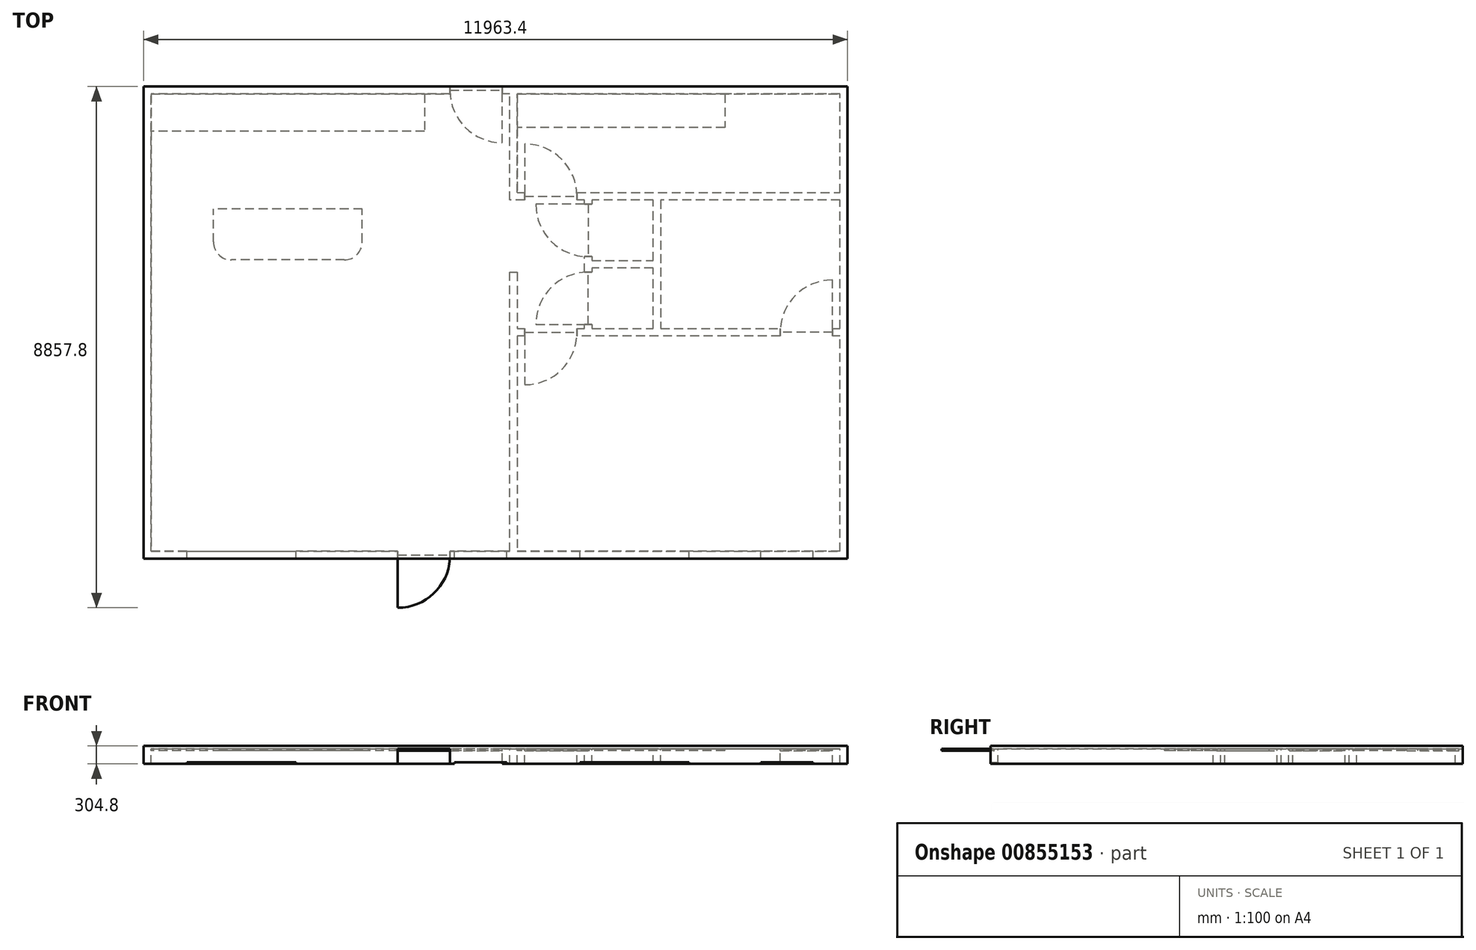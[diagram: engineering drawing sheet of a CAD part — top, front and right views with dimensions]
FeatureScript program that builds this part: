
annotation { "Feature Type Name" : "Feature", "Feature Type Description" : "" }
export const myFeature = defineFeature(function(context is Context, id is Id, definition is map)
    precondition{}
    {
        {
            var Q0;
            Q0=qCreatedBy(makeId("Top.planeOp"),FACE);
            var sketch = newSketch(context, id + "F0", { "sketchPlane" : qUnion([Q0])});
            skLineSegment(sketch, "E0", {"start": v(127, 127) * mm, "end": v(127, 7899.4) * mm});
            skLineSegment(sketch, "E1", {"start": v(127, 7899.4) * mm, "end": v(5207, 7899.4) * mm});
            skLineSegment(sketch, "E2", {"start": v(5207, 7899.4) * mm, "end": v(5207, 8026.4) * mm});
            skLineSegment(sketch, "E3", {"start": v(5207, 8026.4) * mm, "end": v(0, 8026.4) * mm});
            skLineSegment(sketch, "E4", {"start": v(0, 8026.4) * mm, "end": v(0, 0) * mm});
            skLineSegment(sketch, "E5", {"start": v(0, 0) * mm, "end": v(4318, 0) * mm});
            skLineSegment(sketch, "E6", {"start": v(4318, 0) * mm, "end": v(4318, 127) * mm});
            skLineSegment(sketch, "E7", {"start": v(4318, 127) * mm, "end": v(127, 127) * mm});
            skLineSegment(sketch, "E8", {"start": v(6096, 8026.4) * mm, "end": v(6096, 7899.4) * mm});
            skLineSegment(sketch, "E9", {"start": v(6096, 7899.4) * mm, "end": v(6223, 7899.4) * mm});
            skLineSegment(sketch, "E10", {"start": v(6223, 7899.4) * mm, "end": v(6223, 6096) * mm});
            skLineSegment(sketch, "E11", {"start": v(6223, 6096) * mm, "end": v(6477, 6096) * mm});
            skLineSegment(sketch, "E12", {"start": v(6477, 6096) * mm, "end": v(6477, 6223) * mm});
            skLineSegment(sketch, "E13", {"start": v(6477, 6223) * mm, "end": v(6350, 6223) * mm});
            skLineSegment(sketch, "E14", {"start": v(6350, 6223) * mm, "end": v(6350, 7899.4) * mm});
            skLineSegment(sketch, "E15", {"start": v(6350, 7899.4) * mm, "end": v(11836.4, 7899.4) * mm});
            skLineSegment(sketch, "E16", {"start": v(11836.4, 7899.4) * mm, "end": v(11836.4, 6223) * mm});
            skLineSegment(sketch, "E17", {"start": v(11836.4, 6223) * mm, "end": v(7366, 6223) * mm});
            skLineSegment(sketch, "E18", {"start": v(7366, 6223) * mm, "end": v(7366, 6096) * mm});
            skLineSegment(sketch, "E19", {"start": v(7366, 6096) * mm, "end": v(7493, 6096) * mm});
            skLineSegment(sketch, "E20", {"start": v(7493, 6096) * mm, "end": v(7493, 6026.15) * mm});
            skLineSegment(sketch, "E21", {"start": v(7493, 6026.15) * mm, "end": v(7620, 6026.15) * mm});
            skLineSegment(sketch, "E22", {"start": v(7620, 6026.15) * mm, "end": v(7620, 6096) * mm});
            skLineSegment(sketch, "E23", {"start": v(7620, 6096) * mm, "end": v(8661.4, 6096) * mm});
            skLineSegment(sketch, "E24", {"start": v(8661.4, 6096) * mm, "end": v(8661.4, 5067.3) * mm});
            skLineSegment(sketch, "E25", {"start": v(8661.4, 5067.3) * mm, "end": v(7620, 5067.3) * mm});
            skLineSegment(sketch, "E26", {"start": v(7620, 5067.3) * mm, "end": v(7620, 5137.15) * mm});
            skLineSegment(sketch, "E27", {"start": v(7620, 5137.15) * mm, "end": v(7493, 5137.15) * mm});
            skLineSegment(sketch, "E28", {"start": v(7493, 5137.15) * mm, "end": v(7493, 4870.45) * mm});
            skLineSegment(sketch, "E29", {"start": v(7493, 4870.45) * mm, "end": v(7620, 4870.45) * mm});
            skLineSegment(sketch, "E30", {"start": v(7620, 4870.45) * mm, "end": v(7620, 4940.3) * mm});
            skLineSegment(sketch, "E31", {"start": v(7620, 4940.3) * mm, "end": v(8661.4, 4940.3) * mm});
            skLineSegment(sketch, "E32", {"start": v(8661.4, 4940.3) * mm, "end": v(8661.4, 3911.6) * mm});
            skLineSegment(sketch, "E33", {"start": v(8661.4, 3911.6) * mm, "end": v(7620, 3911.6) * mm});
            skLineSegment(sketch, "E34", {"start": v(7620, 3911.6) * mm, "end": v(7620, 3981.45) * mm});
            skLineSegment(sketch, "E35", {"start": v(7620, 3981.45) * mm, "end": v(7493, 3981.45) * mm});
            skLineSegment(sketch, "E36", {"start": v(7493, 3981.45) * mm, "end": v(7493, 3911.6) * mm});
            skLineSegment(sketch, "E37", {"start": v(7493, 3911.6) * mm, "end": v(7366, 3911.6) * mm});
            skLineSegment(sketch, "E38", {"start": v(7366, 3911.6) * mm, "end": v(7366, 3784.6) * mm});
            skLineSegment(sketch, "E39", {"start": v(7366, 3784.6) * mm, "end": v(10820.4, 3784.6) * mm});
            skLineSegment(sketch, "E40", {"start": v(10820.4, 3784.6) * mm, "end": v(10820.4, 3911.6) * mm});
            skLineSegment(sketch, "E41", {"start": v(10820.4, 3911.6) * mm, "end": v(8788.4, 3911.6) * mm});
            skLineSegment(sketch, "E42", {"start": v(8788.4, 3911.6) * mm, "end": v(8788.4, 6096) * mm});
            skLineSegment(sketch, "E43", {"start": v(8788.4, 6096) * mm, "end": v(11836.4, 6096) * mm});
            skLineSegment(sketch, "E44", {"start": v(11836.4, 6096) * mm, "end": v(11836.4, 3911.6) * mm});
            skLineSegment(sketch, "E45", {"start": v(11836.4, 3911.6) * mm, "end": v(11709.4, 3911.6) * mm});
            skLineSegment(sketch, "E46", {"start": v(11709.4, 3911.6) * mm, "end": v(11709.4, 3784.6) * mm});
            skLineSegment(sketch, "E47", {"start": v(11709.4, 3784.6) * mm, "end": v(11836.4, 3784.6) * mm});
            skLineSegment(sketch, "E48", {"start": v(11836.4, 3784.6) * mm, "end": v(11836.4, 127) * mm});
            skLineSegment(sketch, "E49", {"start": v(11836.4, 127) * mm, "end": v(6350, 127) * mm});
            skLineSegment(sketch, "E50", {"start": v(6350, 127) * mm, "end": v(6350, 3784.6) * mm});
            skLineSegment(sketch, "E51", {"start": v(6350, 3784.6) * mm, "end": v(6477, 3784.6) * mm});
            skLineSegment(sketch, "E52", {"start": v(6477, 3784.6) * mm, "end": v(6477, 3911.6) * mm});
            skLineSegment(sketch, "E53", {"start": v(6477, 3911.6) * mm, "end": v(6350, 3911.6) * mm});
            skLineSegment(sketch, "E54", {"start": v(6350, 3911.6) * mm, "end": v(6350, 4870.45) * mm});
            skLineSegment(sketch, "E55", {"start": v(6350, 4870.45) * mm, "end": v(6223, 4870.45) * mm});
            skLineSegment(sketch, "E56", {"start": v(6223, 4870.45) * mm, "end": v(6223, 127) * mm});
            skLineSegment(sketch, "E57", {"start": v(6223, 127) * mm, "end": v(5207, 127) * mm});
            skLineSegment(sketch, "E58", {"start": v(5207, 127) * mm, "end": v(5207, 0) * mm});
            skLineSegment(sketch, "E59", {"start": v(5207, 0) * mm, "end": v(11963.4, 0) * mm});
            skLineSegment(sketch, "E60", {"start": v(11963.4, 0) * mm, "end": v(11963.4, 8026.4) * mm});
            skLineSegment(sketch, "E61", {"start": v(11963.4, 8026.4) * mm, "end": v(6096, 8026.4) * mm});
            skLineSegment(sketch, "E62", {"start": v(7556.5, 6026.15) * mm, "end": v(7556.5, 5137.15) * mm, "construction": true});
            skLineSegment(sketch, "E63", {"start": v(7556.5, 4870.45) * mm, "end": v(7556.5, 3981.45) * mm, "construction": true});
            skLineSegment(sketch, "E64", {"start": v(6477, 6159.5) * mm, "end": v(7366, 6159.5) * mm, "construction": true});
            skLineSegment(sketch, "E65", {"start": v(6477, 3848.1) * mm, "end": v(7366, 3848.1) * mm, "construction": true});
            skLineSegment(sketch, "E66", {"start": v(10820.4, 3848.1) * mm, "end": v(11709.4, 3848.1) * mm, "construction": true});
            skLineSegment(sketch, "E67", {"start": v(4318, 63.5) * mm, "end": v(5207, 63.5) * mm, "construction": true});
            skLineSegment(sketch, "E68", {"start": v(5207, 7962.9) * mm, "end": v(6096, 7962.9) * mm, "construction": true});
            skSolve(sketch);
        }
        {
            var Q0;
            Q0 = qSketchRegion(id + "F0", true);
            extrude(context, id + "F1", {"entities" : qUnion([Q0]), "oppositeDirection" : true, "depth" : 304.8 * mm, "offsetDistance" : 30.48 * mm});
        }
        {
            var Q0;
            Q0=makeQuery(id+"F1.opExtrude","CAP_FACE",FACE,{"disambiguationData":[OSD([sQuery(id+"F0.wireOp",EDGE,"E8"),sQuery(id+"F0.wireOp",EDGE,"E9"),sQuery(id+"F0.wireOp",EDGE,"E10"),sQuery(id+"F0.wireOp",EDGE,"E11"),sQuery(id+"F0.wireOp",EDGE,"E12"),sQuery(id+"F0.wireOp",EDGE,"E13"),sQuery(id+"F0.wireOp",EDGE,"E14"),sQuery(id+"F0.wireOp",EDGE,"E15"),sQuery(id+"F0.wireOp",EDGE,"E16"),sQuery(id+"F0.wireOp",EDGE,"E17"),sQuery(id+"F0.wireOp",EDGE,"E18"),sQuery(id+"F0.wireOp",EDGE,"E19"),sQuery(id+"F0.wireOp",EDGE,"E20"),sQuery(id+"F0.wireOp",EDGE,"E21"),sQuery(id+"F0.wireOp",EDGE,"E22"),sQuery(id+"F0.wireOp",EDGE,"E23"),sQuery(id+"F0.wireOp",EDGE,"E24"),sQuery(id+"F0.wireOp",EDGE,"E25"),sQuery(id+"F0.wireOp",EDGE,"E26"),sQuery(id+"F0.wireOp",EDGE,"E27"),sQuery(id+"F0.wireOp",EDGE,"E28"),sQuery(id+"F0.wireOp",EDGE,"E29"),sQuery(id+"F0.wireOp",EDGE,"E30"),sQuery(id+"F0.wireOp",EDGE,"E31"),sQuery(id+"F0.wireOp",EDGE,"E32"),sQuery(id+"F0.wireOp",EDGE,"E33"),sQuery(id+"F0.wireOp",EDGE,"E34"),sQuery(id+"F0.wireOp",EDGE,"E35"),sQuery(id+"F0.wireOp",EDGE,"E36"),sQuery(id+"F0.wireOp",EDGE,"E37"),sQuery(id+"F0.wireOp",EDGE,"E38"),sQuery(id+"F0.wireOp",EDGE,"E39"),sQuery(id+"F0.wireOp",EDGE,"E40"),sQuery(id+"F0.wireOp",EDGE,"E41"),sQuery(id+"F0.wireOp",EDGE,"E42"),sQuery(id+"F0.wireOp",EDGE,"E43"),sQuery(id+"F0.wireOp",EDGE,"E44"),sQuery(id+"F0.wireOp",EDGE,"E45"),sQuery(id+"F0.wireOp",EDGE,"E46"),sQuery(id+"F0.wireOp",EDGE,"E47"),sQuery(id+"F0.wireOp",EDGE,"E48"),sQuery(id+"F0.wireOp",EDGE,"E49"),sQuery(id+"F0.wireOp",EDGE,"E50"),sQuery(id+"F0.wireOp",EDGE,"E51"),sQuery(id+"F0.wireOp",EDGE,"E52"),sQuery(id+"F0.wireOp",EDGE,"E53"),sQuery(id+"F0.wireOp",EDGE,"E54"),sQuery(id+"F0.wireOp",EDGE,"E55"),sQuery(id+"F0.wireOp",EDGE,"E56"),sQuery(id+"F0.wireOp",EDGE,"E57"),sQuery(id+"F0.wireOp",EDGE,"E58"),sQuery(id+"F0.wireOp",EDGE,"E59"),sQuery(id+"F0.wireOp",EDGE,"E60"),sQuery(id+"F0.wireOp",EDGE,"E61")])],"isStart":true});
            var sketch = newSketch(context, id + "F2", { "sketchPlane" : qUnion([Q0])});
            skLineSegment(sketch, "E69.bottom", {"start": v(11963.4, 0) * mm, "end": v(0, 0) * mm});
            skLineSegment(sketch, "E69.top", {"start": v(11963.4, 8026.4) * mm, "end": v(0, 8026.4) * mm});
            skLineSegment(sketch, "E69.left", {"start": v(11963.4, 0) * mm, "end": v(11963.4, 8026.4) * mm});
            skLineSegment(sketch, "E69.right", {"start": v(0, 0) * mm, "end": v(0, 8026.4) * mm});
            skSolve(sketch);
        }
        {
            var Q0;
            Q0 = qSketchRegion(id + "F2", true);
            var Q1;
            Q1=makeQuery(id+"FFcsoDlnS58ntc3_0.opExtrude","CAP_FACE",FACE,{"disambiguationData":[OSD([sQuery(id+"F6g3n0T531UEJvB_0.wireOp",EDGE,"5hh6yJa4-IKVP-9uf4-aUaf-O9rZmwUvxoOS.bottom"),sQuery(id+"F6g3n0T531UEJvB_0.wireOp",EDGE,"5hh6yJa4-IKVP-9uf4-aUaf-O9rZmwUvxoOS.top"),sQuery(id+"F6g3n0T531UEJvB_0.wireOp",EDGE,"5hh6yJa4-IKVP-9uf4-aUaf-O9rZmwUvxoOS.left"),sQuery(id+"F6g3n0T531UEJvB_0.wireOp",EDGE,"5hh6yJa4-IKVP-9uf4-aUaf-O9rZmwUvxoOS.right")])],"isStart":false});
            extrude(context, id + "F3", {"entities" : qUnion([Q0]), "operationType" : NewBodyOperationType.ADD, "oppositeDirection" : true, "depth" : 50.8 * mm, "endBoundEntityFace" : qUnion([Q1]), "offsetDistance" : 30.48 * mm});
        }
        {
            var Q0;
            Q0=makeQuery(id+"F1.opExtrude","CAP_FACE",FACE,{"disambiguationData":[OSD([sQuery(id+"F0.wireOp",EDGE,"E8"),sQuery(id+"F0.wireOp",EDGE,"E9"),sQuery(id+"F0.wireOp",EDGE,"E10"),sQuery(id+"F0.wireOp",EDGE,"E11"),sQuery(id+"F0.wireOp",EDGE,"E12"),sQuery(id+"F0.wireOp",EDGE,"E13"),sQuery(id+"F0.wireOp",EDGE,"E14"),sQuery(id+"F0.wireOp",EDGE,"E15"),sQuery(id+"F0.wireOp",EDGE,"E16"),sQuery(id+"F0.wireOp",EDGE,"E17"),sQuery(id+"F0.wireOp",EDGE,"E18"),sQuery(id+"F0.wireOp",EDGE,"E19"),sQuery(id+"F0.wireOp",EDGE,"E20"),sQuery(id+"F0.wireOp",EDGE,"E21"),sQuery(id+"F0.wireOp",EDGE,"E22"),sQuery(id+"F0.wireOp",EDGE,"E23"),sQuery(id+"F0.wireOp",EDGE,"E24"),sQuery(id+"F0.wireOp",EDGE,"E25"),sQuery(id+"F0.wireOp",EDGE,"E26"),sQuery(id+"F0.wireOp",EDGE,"E27"),sQuery(id+"F0.wireOp",EDGE,"E28"),sQuery(id+"F0.wireOp",EDGE,"E29"),sQuery(id+"F0.wireOp",EDGE,"E30"),sQuery(id+"F0.wireOp",EDGE,"E31"),sQuery(id+"F0.wireOp",EDGE,"E32"),sQuery(id+"F0.wireOp",EDGE,"E33"),sQuery(id+"F0.wireOp",EDGE,"E34"),sQuery(id+"F0.wireOp",EDGE,"E35"),sQuery(id+"F0.wireOp",EDGE,"E36"),sQuery(id+"F0.wireOp",EDGE,"E37"),sQuery(id+"F0.wireOp",EDGE,"E38"),sQuery(id+"F0.wireOp",EDGE,"E39"),sQuery(id+"F0.wireOp",EDGE,"E40"),sQuery(id+"F0.wireOp",EDGE,"E41"),sQuery(id+"F0.wireOp",EDGE,"E42"),sQuery(id+"F0.wireOp",EDGE,"E43"),sQuery(id+"F0.wireOp",EDGE,"E44"),sQuery(id+"F0.wireOp",EDGE,"E45"),sQuery(id+"F0.wireOp",EDGE,"E46"),sQuery(id+"F0.wireOp",EDGE,"E47"),sQuery(id+"F0.wireOp",EDGE,"E48"),sQuery(id+"F0.wireOp",EDGE,"E49"),sQuery(id+"F0.wireOp",EDGE,"E50"),sQuery(id+"F0.wireOp",EDGE,"E51"),sQuery(id+"F0.wireOp",EDGE,"E52"),sQuery(id+"F0.wireOp",EDGE,"E53"),sQuery(id+"F0.wireOp",EDGE,"E54"),sQuery(id+"F0.wireOp",EDGE,"E55"),sQuery(id+"F0.wireOp",EDGE,"E56"),sQuery(id+"F0.wireOp",EDGE,"E57"),sQuery(id+"F0.wireOp",EDGE,"E58"),sQuery(id+"F0.wireOp",EDGE,"E59"),sQuery(id+"F0.wireOp",EDGE,"E60"),sQuery(id+"F0.wireOp",EDGE,"E61")])],"isStart":false});
            var sketch = newSketch(context, id + "F4", { "sketchPlane" : qUnion([Q0])});
            skLineSegment(sketch, "E70.bottom", {"start": v(5283.2, 0) * mm, "end": v(6172.2, 0) * mm});
            skLineSegment(sketch, "E70.top", {"start": v(5283.2, -127) * mm, "end": v(6172.2, -127) * mm});
            skLineSegment(sketch, "E70.left", {"start": v(5283.2, 0) * mm, "end": v(5283.2, -127) * mm});
            skLineSegment(sketch, "E70.right", {"start": v(6172.2, 0) * mm, "end": v(6172.2, -127) * mm});
            skLineSegment(sketch, "E71.bottom", {"start": v(7416.8, 0) * mm, "end": v(9271, 0) * mm});
            skLineSegment(sketch, "E71.top", {"start": v(7416.8, -127) * mm, "end": v(9271, -127) * mm});
            skLineSegment(sketch, "E71.left", {"start": v(7416.8, 0) * mm, "end": v(7416.8, -127) * mm});
            skLineSegment(sketch, "E71.right", {"start": v(9271, 0) * mm, "end": v(9271, -127) * mm});
            skLineSegment(sketch, "E72.bottom", {"start": v(10490.2, 0) * mm, "end": v(11379.2, 0) * mm});
            skLineSegment(sketch, "E72.top", {"start": v(10490.2, -127) * mm, "end": v(11379.2, -127) * mm});
            skLineSegment(sketch, "E72.left", {"start": v(10490.2, 0) * mm, "end": v(10490.2, -127) * mm});
            skLineSegment(sketch, "E72.right", {"start": v(11379.2, 0) * mm, "end": v(11379.2, -127) * mm});
            skLineSegment(sketch, "E73.bottom", {"start": v(736.6, 0) * mm, "end": v(2590.8, 0) * mm});
            skLineSegment(sketch, "E73.top", {"start": v(736.6, -127) * mm, "end": v(2590.8, -127) * mm});
            skLineSegment(sketch, "E73.left", {"start": v(736.6, 0) * mm, "end": v(736.6, -127) * mm});
            skLineSegment(sketch, "E73.right", {"start": v(2590.8, 0) * mm, "end": v(2590.8, -127) * mm});
            skSolve(sketch);
        }
        {
            var Q0;
            Q0 = qSketchRegion(id + "F4", true);
            extrude(context, id + "F5", {"entities" : qUnion([Q0]), "operationType" : NewBodyOperationType.REMOVE, "oppositeDirection" : true, "depth" : 30.48 * mm, "offsetDistance" : 30.48 * mm});
        }
        {
            var Q0;
            Q0=makeQuery(id+"F3.opExtrude","CAP_FACE",FACE,{"disambiguationData":[OSD([sQuery(id+"F2.wireOp",EDGE,"E69.bottom"),sQuery(id+"F2.wireOp",EDGE,"E69.top"),sQuery(id+"F2.wireOp",EDGE,"E69.left"),sQuery(id+"F2.wireOp",EDGE,"E69.right")])],"isStart":false});
            var sketch = newSketch(context, id + "F6", { "sketchPlane" : qUnion([Q0])});
            skLineSegment(sketch, "E74.bottom", {"start": v(3411.22, -5080) * mm, "end": v(1490.98, -5080) * mm});
            skLineSegment(sketch, "E74.top", {"start": v(3716.02, -5943.6) * mm, "end": v(1186.18, -5943.6) * mm});
            skLineSegment(sketch, "E74.left", {"start": v(3716.02, -5384.8) * mm, "end": v(3716.02, -5943.6) * mm});
            skLineSegment(sketch, "E74.right", {"start": v(1186.18, -5384.8) * mm, "end": v(1186.18, -5943.6) * mm});
            skPoint(sketch, "E74.middle", {"position": v(2451.1, -5511.8) * mm});
            skLineSegment(sketch, "E75.bottom", {"start": v(4775.2, -7899.4) * mm, "end": v(127, -7899.4) * mm});
            skLineSegment(sketch, "E75.top", {"start": v(4775.2, -7264.4) * mm, "end": v(127, -7264.4) * mm});
            skLineSegment(sketch, "E75.left", {"start": v(4775.2, -7899.4) * mm, "end": v(4775.2, -7264.4) * mm});
            skLineSegment(sketch, "E75.right", {"start": v(127, -7899.4) * mm, "end": v(127, -7264.4) * mm});
            skPoint(sketch, "E75.middle", {"position": v(2451.1, -7581.9) * mm});
            skLineSegment(sketch, "E76.bottom", {"start": v(9880.6, -7899.4) * mm, "end": v(6350, -7899.4) * mm});
            skLineSegment(sketch, "E76.top", {"start": v(9880.6, -7327.9) * mm, "end": v(6350, -7327.9) * mm});
            skLineSegment(sketch, "E76.left", {"start": v(9880.6, -7899.4) * mm, "end": v(9880.6, -7327.9) * mm});
            skLineSegment(sketch, "E76.right", {"start": v(6350, -7899.4) * mm, "end": v(6350, -7327.9) * mm});
            skPoint(sketch, "E76.middle", {"position": v(8115.3, -7613.65) * mm});
            skPoint(sketch, "E77.visualSharp", {"position": v(1186.18, -5080) * mm});
            skArc(sketch, "E77.filletArc", {"start": v(1490.98, -5080) * mm, "mid": v(1275.45, -5169.27) * mm, "end": v(1186.18, -5384.8) * mm});
            skPoint(sketch, "E78.visualSharp", {"position": v(3716.02, -5080) * mm});
            skArc(sketch, "E78.filletArc", {"start": v(3716.02, -5384.8) * mm, "mid": v(3626.75, -5169.27) * mm, "end": v(3411.22, -5080) * mm});
            skLineSegment(sketch, "E79.bottom", {"start": v(4318, -63.5) * mm, "end": v(5207, -63.5) * mm});
            skLineSegment(sketch, "E79.top", {"start": v(4318, 831.4) * mm, "end": v(4323.08, 831.4) * mm});
            skLineSegment(sketch, "E79.left", {"start": v(4318, -63.5) * mm, "end": v(4318, 831.4) * mm});
            skLineSegment(sketch, "E79.right", {"start": v(5207, -63.5) * mm, "end": v(5207, -52.52) * mm});
            skLineSegment(sketch, "E80.bottom", {"start": v(6477, -3848.1) * mm, "end": v(7366, -3848.1) * mm});
            skLineSegment(sketch, "E80.top", {"start": v(6477, -2959.1) * mm, "end": v(6482.08, -2959.1) * mm});
            skLineSegment(sketch, "E80.left", {"start": v(6477, -3848.1) * mm, "end": v(6477, -2959.1) * mm});
            skLineSegment(sketch, "E80.right", {"start": v(7366, -3848.1) * mm, "end": v(7366, -3843.02) * mm});
            skLineSegment(sketch, "E81.bottom", {"start": v(7556.5, -6026.15) * mm, "end": v(6667.5, -6026.15) * mm});
            skLineSegment(sketch, "E81.top", {"start": v(7556.5, -5137.15) * mm, "end": v(7551.42, -5137.15) * mm});
            skLineSegment(sketch, "E81.left", {"start": v(7556.5, -6026.15) * mm, "end": v(7556.5, -5137.15) * mm});
            skLineSegment(sketch, "E81.right", {"start": v(6667.5, -6026.15) * mm, "end": v(6667.5, -6021.07) * mm});
            skLineSegment(sketch, "E82.bottom", {"start": v(7556.5, -3981.45) * mm, "end": v(6667.5, -3981.45) * mm});
            skLineSegment(sketch, "E82.top", {"start": v(7556.5, -4870.45) * mm, "end": v(7551.42, -4870.45) * mm});
            skLineSegment(sketch, "E82.left", {"start": v(7556.5, -3981.45) * mm, "end": v(7556.5, -4870.45) * mm});
            skLineSegment(sketch, "E82.right", {"start": v(6667.5, -3981.45) * mm, "end": v(6667.5, -3986.53) * mm});
            skLineSegment(sketch, "E83.bottom", {"start": v(6477, -6159.5) * mm, "end": v(7366, -6159.5) * mm});
            skLineSegment(sketch, "E83.top", {"start": v(6477, -7048.5) * mm, "end": v(6482.08, -7048.5) * mm});
            skLineSegment(sketch, "E83.left", {"start": v(6477, -6159.5) * mm, "end": v(6477, -7048.5) * mm});
            skLineSegment(sketch, "E83.right", {"start": v(7366, -6159.5) * mm, "end": v(7366, -6164.58) * mm});
            skLineSegment(sketch, "E84.bottom", {"start": v(11709.4, -3848.1) * mm, "end": v(10820.4, -3848.1) * mm});
            skLineSegment(sketch, "E84.top", {"start": v(11709.4, -4737.1) * mm, "end": v(11704.32, -4737.1) * mm});
            skLineSegment(sketch, "E84.left", {"start": v(11709.4, -3848.1) * mm, "end": v(11709.4, -4737.1) * mm});
            skLineSegment(sketch, "E84.right", {"start": v(10820.4, -3848.1) * mm, "end": v(10820.4, -3853.18) * mm});
            skPoint(sketch, "E85.visualSharp", {"position": v(5207, 831.4) * mm});
            skArc(sketch, "E85.filletArc", {"start": v(5207, -52.52) * mm, "mid": v(4948.1, 572.5) * mm, "end": v(4323.08, 831.4) * mm});
            skPoint(sketch, "E86.visualSharp", {"position": v(7366, -2959.1) * mm});
            skArc(sketch, "E86.filletArc", {"start": v(7366, -3843.02) * mm, "mid": v(7107.1, -3218) * mm, "end": v(6482.08, -2959.1) * mm});
            skPoint(sketch, "E87.visualSharp", {"position": v(6667.5, -4870.45) * mm});
            skArc(sketch, "E87.filletArc", {"start": v(6667.5, -3986.53) * mm, "mid": v(6926.4, -4611.56) * mm, "end": v(7551.42, -4870.45) * mm});
            skPoint(sketch, "E88.visualSharp", {"position": v(6667.5, -5137.15) * mm});
            skArc(sketch, "E88.filletArc", {"start": v(7551.42, -5137.15) * mm, "mid": v(6926.4, -5396.04) * mm, "end": v(6667.5, -6021.07) * mm});
            skPoint(sketch, "E89.visualSharp", {"position": v(10820.4, -4737.1) * mm});
            skArc(sketch, "E89.filletArc", {"start": v(10820.4, -3853.18) * mm, "mid": v(11079.3, -4478.2) * mm, "end": v(11704.32, -4737.1) * mm});
            skPoint(sketch, "E90.visualSharp", {"position": v(7366, -7048.5) * mm});
            skArc(sketch, "E90.filletArc", {"start": v(6482.08, -7048.5) * mm, "mid": v(7107.1, -6789.6) * mm, "end": v(7366, -6164.58) * mm});
            skPoint(sketch, "E91.oppositeSnap0", {"position": v(6096, -7962.9) * mm});
            skLineSegment(sketch, "E91.bottom", {"start": v(5207, -7962.9) * mm, "end": v(6096, -7962.9) * mm});
            skLineSegment(sketch, "E91.top", {"start": v(6090.92, -7073.9) * mm, "end": v(6096, -7073.9) * mm});
            skLineSegment(sketch, "E91.left", {"start": v(5207, -7962.9) * mm, "end": v(5207, -7957.82) * mm});
            skLineSegment(sketch, "E91.right", {"start": v(6096, -7962.9) * mm, "end": v(6096, -7073.9) * mm});
            skPoint(sketch, "E92.visualSharp", {"position": v(5207, -7073.9) * mm});
            skArc(sketch, "E92.filletArc", {"start": v(6090.92, -7073.9) * mm, "mid": v(5465.9, -7332.8) * mm, "end": v(5207, -7957.82) * mm});
            skSolve(sketch);
        }
        {
            var Q0;
            Q0 = qSketchRegion(id + "F6", true);
            extrude(context, id + "F7", {"entities" : qUnion([Q0]), "operationType" : NewBodyOperationType.ADD, "depth" : 30.48 * mm, "offsetDistance" : 30.48 * mm});
        }
    });
